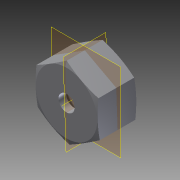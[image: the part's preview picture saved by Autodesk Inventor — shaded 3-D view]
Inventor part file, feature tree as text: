
AUTODESK INVENTOR PART (.ipt)
format: ipt  version: 2014 (Build 180170000, 170)  size: 135,168 bytes
history: native  units: in
note: dims shown in document units (in); Inventor stores cm internally (conversion verified against a paired STEP export)
features: sketch x4, plane x3, extrude x3, reference x2, thread x1, other x1, revolve x1, mirror x1
ambient origin geometry x8: Origin, YZ Plane, XZ Plane, XY Plane, X Axis, Y Axis, Z Axis, Center Point
bodies: Body1 (feature_tree)
feature tree (16):
  plane  "Work Plane3"
  extrude  "Extrusion2"  Depth=0.5in
  extrude  "Extrusion3"  Depth=0.375in TaperAngle=0.0deg
  extrude  "Extrusion4"  TaperAngle=90.0deg  [1 undecoded]
  thread  "Thread1"  [1 undecoded]
  plane  "Work Plane4"
  other  "Work Axis4"
  revolve  "Revolution2"  [1 undecoded]
  plane  "Work Plane5"
  mirror  "Mirror1"
  sketch  "Sketch6"  dims[d3=0.3125in d4=0.0in d5=0.5in]
  sketch  "Sketch7"  dims[d6=0.25in d7=-0.0123in d8=0.375in d9=0.0in]
  reference  "Reference1"
  sketch  "Sketch8"  dims[d10=0.392in d11=0.0in d12=90.0deg d13=0.045in]
  reference  "Reference2"
  sketch  "Sketch9"
note: 3 required parameter values undecoded (feature->parameter linkage not recoverable at this tier; creation-order binding heuristic only, values carry confidence <= 0.55)
